# Revit family: Haworth_Atwell_HipChair
name_source: partatom
category: Furniture
revit_build: Autodesk Revit 2018 (Build: 20170223_1515(x64)
units: mm (PartAtom-declared; Revit-internal decimal feet)

## family parameters
Always vertical = Yes
Cut with Voids When Loaded = No
OmniClass Number = 23.40.20.00
OmniClass Title = General Furniture and Specialties
Room Calculation Point = No
Shared = No
Work Plane-Based = No

## types (1)
- HE901-HC - 25w
    Actual Depth = 2' - 6"
    Actual Height = 3' - 7"
    Actual Width = 2' - 1"
    Arm Cap = No
    Assembly Code = E2020200
    Description = Hip Chair
    Hardware Finish = Haworth _ Metal _ Brushed Aluminum
    Manufacturer = Haworth
    Model = Haworth Atwell
    Size = Verify Final Dim. w/ Haworth
    Sustainability Info = https://www.haworth.com
    URL = http://haworth.com
    URL - Product = http://healthcare.haworth.com
    Version = 1
    Warranty = http://healthcare.haworth.com

## geometry (parser evidence)
native form markers: Sweep x2
no freeform markers — native parametric forms only
